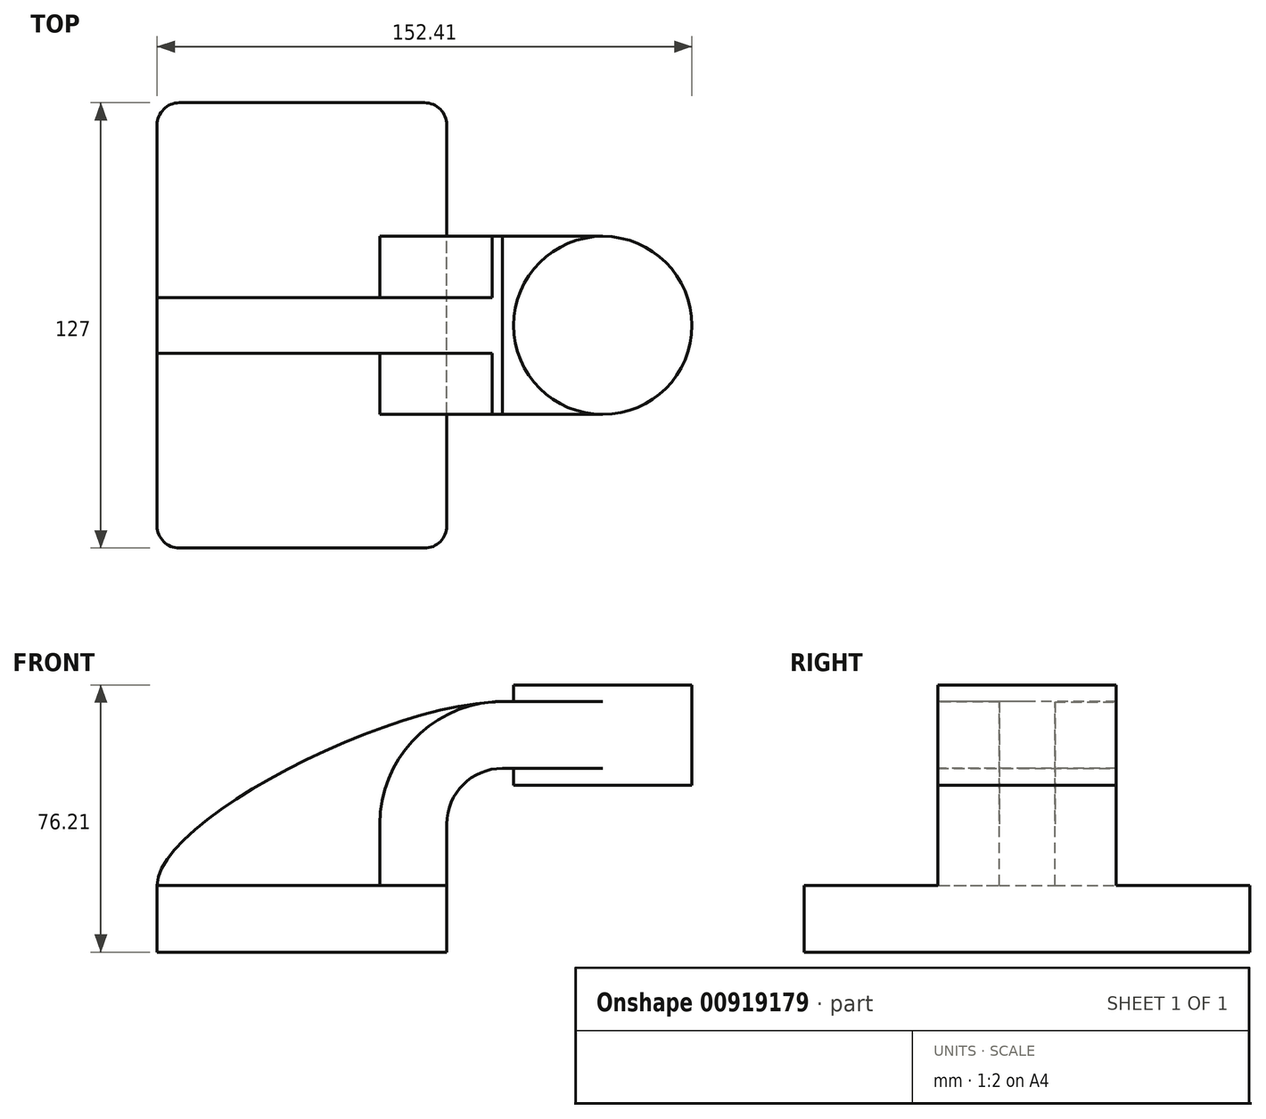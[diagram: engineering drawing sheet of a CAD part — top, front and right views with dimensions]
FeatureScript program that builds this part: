
annotation { "Feature Type Name" : "Feature", "Feature Type Description" : "" }
export const myFeature = defineFeature(function(context is Context, id is Id, definition is map)
    precondition{}
    {
        {
            var Q0;
            Q0=qCreatedBy(makeId("Front.planeOp"),FACE);
            var sketch = newSketch(context, id + "F0", { "sketchPlane" : qUnion([Q0])});
            skLineSegment(sketch, "E0.bottom", {"start": v(-41.28, 9.52) * mm, "end": v(41.28, 9.53) * mm});
            skLineSegment(sketch, "E0.top", {"start": v(-41.28, -9.53) * mm, "end": v(41.28, -9.53) * mm});
            skLineSegment(sketch, "E0.left", {"start": v(-41.28, 9.52) * mm, "end": v(-41.28, -9.53) * mm});
            skLineSegment(sketch, "E0.right", {"start": v(41.28, 9.53) * mm, "end": v(41.28, -9.52) * mm});
            skPoint(sketch, "E0.middle", {"position": v(0, 0) * mm});
            skLineSegment(sketch, "E1.bottom", {"start": v(60.33, 38.1) * mm, "end": v(111.12, 38.1) * mm});
            skLineSegment(sketch, "E1.top", {"start": v(60.32, 66.68) * mm, "end": v(111.12, 66.68) * mm});
            skLineSegment(sketch, "E1.left", {"start": v(60.32, 38.1) * mm, "end": v(60.32, 66.68) * mm});
            skLineSegment(sketch, "E1.right", {"start": v(111.12, 38.1) * mm, "end": v(111.12, 66.68) * mm});
            skPoint(sketch, "E1.middle", {"position": v(85.72, 52.39) * mm});
            skLineSegment(sketch, "E2", {"start": v(41.27, 9.53) * mm, "end": v(41.27, 27) * mm});
            skArc(sketch, "E3", {"start": v(41.27, 27) * mm, "mid": v(45.92, 38.23) * mm, "end": v(57.15, 42.88) * mm});
            skLineSegment(sketch, "E4", {"start": v(57.15, 42.88) * mm, "end": v(85.72, 42.88) * mm});
            skLineSegment(sketch, "E5.0", {"start": v(57.15, 61.93) * mm, "end": v(85.72, 61.93) * mm});
            skArc(sketch, "E5.1", {"start": v(22.22, 27) * mm, "mid": v(32.45, 51.7) * mm, "end": v(57.15, 61.93) * mm});
            skLineSegment(sketch, "E5.2", {"start": v(22.22, 9.53) * mm, "end": v(22.22, 27) * mm});
            skLineSegment(sketch, "E6", {"start": v(85.72, 42.88) * mm, "end": v(85.72, 61.93) * mm});
            skFitSpline(sketch, "E7", {"points": [v(-41.28, 9.52) * mm, v(57.15, 61.93) * mm], "startDerivative": vector(-0.64, 52.82) * mm, "endDerivative": vector(103.1, 1.65) * mm});
            skPoint(sketch, "E8", {"position": v(85.72, 66.68) * mm});
            skLineSegment(sketch, "E9", {"start": v(85.72, 61.93) * mm, "end": v(85.72, 66.68) * mm});
            skLineSegment(sketch, "E10", {"start": v(85.73, 42.88) * mm, "end": v(85.72, 38.1) * mm});
            skSolve(sketch);
        }
        {
            var Q0;
            Q0=makeQuery(id+"F0.imprint","IMPRINT",FACE,{"disambiguationData":[TD([[makeQuery(id+"F0.imprint","IMPRINT",EDGE,{"derivedFrom":sQuery(id+"F0.wireOp",EDGE,"E0.top")}),1.0]])]});
            extrude(context, id + "F1", {"entities" : qUnion([Q0]), "endBound" : BoundingType.SYMMETRIC, "depth" : 127 * mm, "offsetDistance" : 25.4 * mm});
        }
        {
            var Q0;
            {var subQ1=sQuery(id+"F0.wireOp",EDGE,"E2");Q0=makeQuery(id+"F0.imprint","IMPRINT",FACE,{"disambiguationData":[TD([[makeQuery(id+"F0.imprint","IMPRINT",EDGE,{"derivedFrom":subQ1}),1.0]])]});}
            var Q1;
            {var subQ5=sQuery(id+"F0.wireOp",EDGE,"E6");Q1=makeQuery(id+"F0.imprint","IMPRINT",FACE,{"disambiguationData":[TD([[makeQuery(id+"F0.imprint","IMPRINT",EDGE,{"derivedFrom":subQ5}),1.0]])]});}
            extrude(context, id + "F2", {"entities" : qUnion([Q0, Q1]), "operationType" : NewBodyOperationType.ADD, "endBound" : BoundingType.SYMMETRIC, "depth" : 50.8 * mm, "offsetDistance" : 25.4 * mm});
        }
        {
            var Q0;
            {var subQ3=sQuery(id+"F0.wireOp",EDGE,"E5.2");Q0=makeQuery(id+"F0.imprint","IMPRINT",FACE,{"disambiguationData":[TD([[makeQuery(id+"F0.imprint","IMPRINT",EDGE,{"derivedFrom":subQ3}),1.0]])]});}
            extrude(context, id + "F3", {"entities" : qUnion([Q0]), "operationType" : NewBodyOperationType.ADD, "endBound" : BoundingType.SYMMETRIC, "depth" : 15.88 * mm, "offsetDistance" : 25.4 * mm});
        }
        {
            var Q0;
            {var subQ0=sQuery(id+"F0.wireOp",EDGE,"E1.right");Q0=makeQuery(id+"F0.imprint","IMPRINT",FACE,{"disambiguationData":[TD([[makeQuery(id+"F0.imprint","IMPRINT",EDGE,{"derivedFrom":subQ0}),1.0]])]});}
            var Q1;
            Q1=sQuery(id+"F0.wireOp",EDGE,"E6");
            revolve(context, id + "F4", {"operationType" : NewBodyOperationType.ADD, "surfaceOperationType" : NewSurfaceOperationType.NEW, "entities" : qUnion([Q0]), "axis" : qUnion([Q1]), "revolveType" : RevolveType.FULL});
        }
        {
            var Q0;
            Q0=makeQuery(id+"F1.opExtrude","CAP_EDGE",EDGE,{"disambiguationData":[OSD([sQuery(id+"F0.wireOp",EDGE,"E0.left")])],"isStart":false});
            var Q1;
            Q1=makeQuery(id+"F1.opExtrude","CAP_EDGE",EDGE,{"disambiguationData":[OSD([sQuery(id+"F0.wireOp",EDGE,"E0.right")])],"isStart":false});
            var Q2;
            Q2=makeQuery(id+"F1.opExtrude","CAP_EDGE",EDGE,{"disambiguationData":[OSD([sQuery(id+"F0.wireOp",EDGE,"E0.left")])],"isStart":true});
            var Q3;
            Q3=makeQuery(id+"F1.opExtrude","CAP_EDGE",EDGE,{"disambiguationData":[OSD([sQuery(id+"F0.wireOp",EDGE,"E0.right")])],"isStart":true});
            fillet(context, id + "F5", {"entities" : qUnion([Q0, Q1, Q2, Q3]), "radius" : 6.35 * mm, "tangentPropagation" : true, "allowEdgeOverflow" : false});
        }
    });
